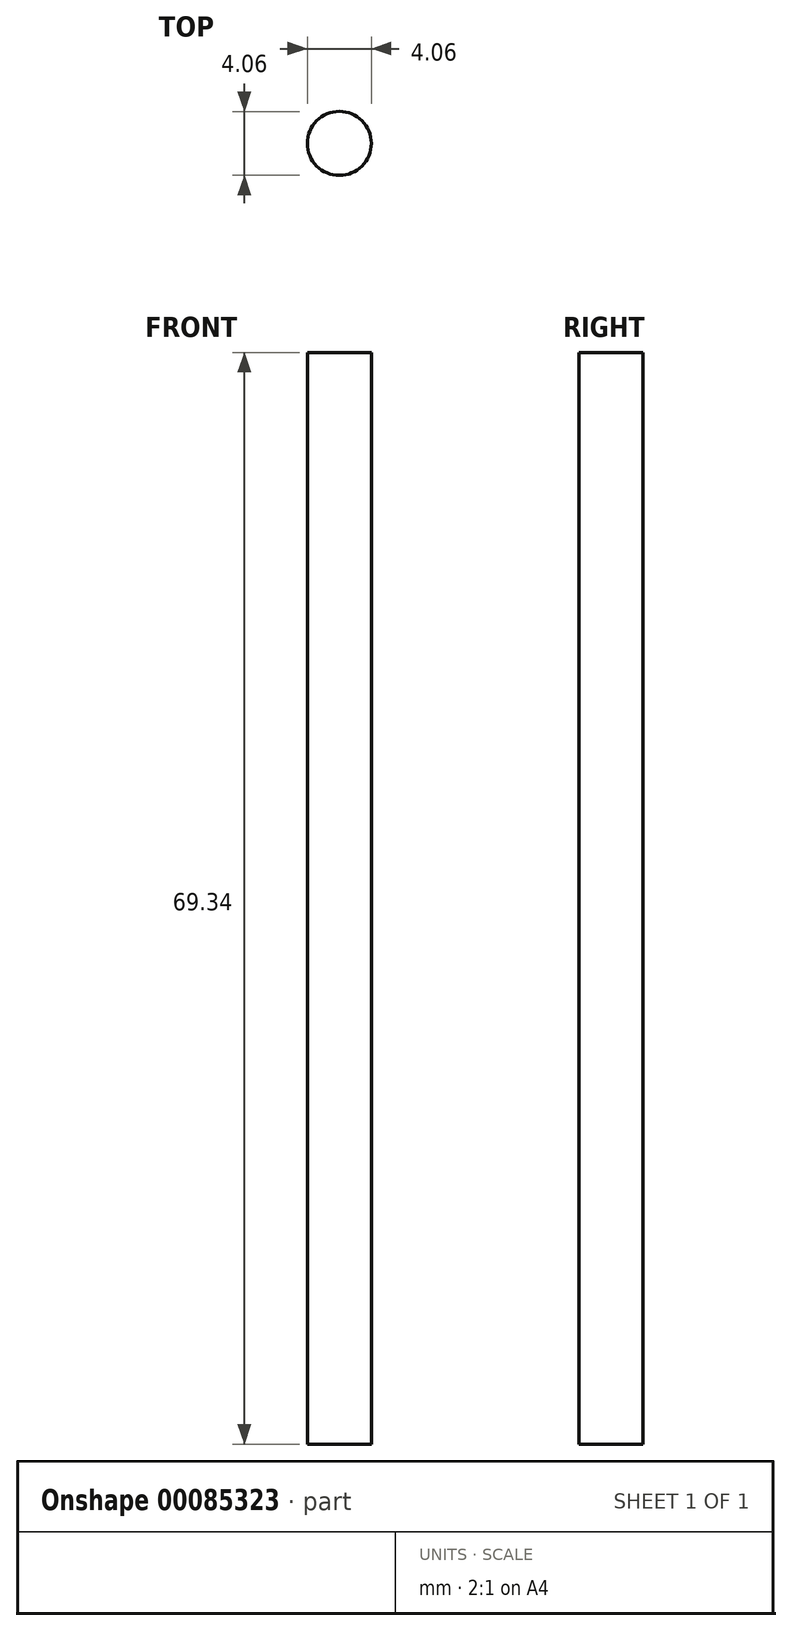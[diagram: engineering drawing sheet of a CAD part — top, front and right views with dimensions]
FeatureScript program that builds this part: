
annotation { "Feature Type Name" : "Feature", "Feature Type Description" : "" }
export const myFeature = defineFeature(function(context is Context, id is Id, definition is map)
    precondition{}
    {
        {
            var Q0;
            Q0=qCreatedBy(makeId("Top.planeOp"),FACE);
            var sketch = newSketch(context, id + "F0", { "sketchPlane" : qUnion([Q0])});
            skCircle(sketch, "E0", {"center": v(0, 0) * mm, "radius": 2.03 * mm});
            skSolve(sketch);
        }
        {
            var Q0;
            Q0 = qSketchRegion(id + "F0", true);
            extrude(context, id + "F1", {"entities" : qUnion([Q0]), "depth" : 69.34 * mm});
        }
    });
